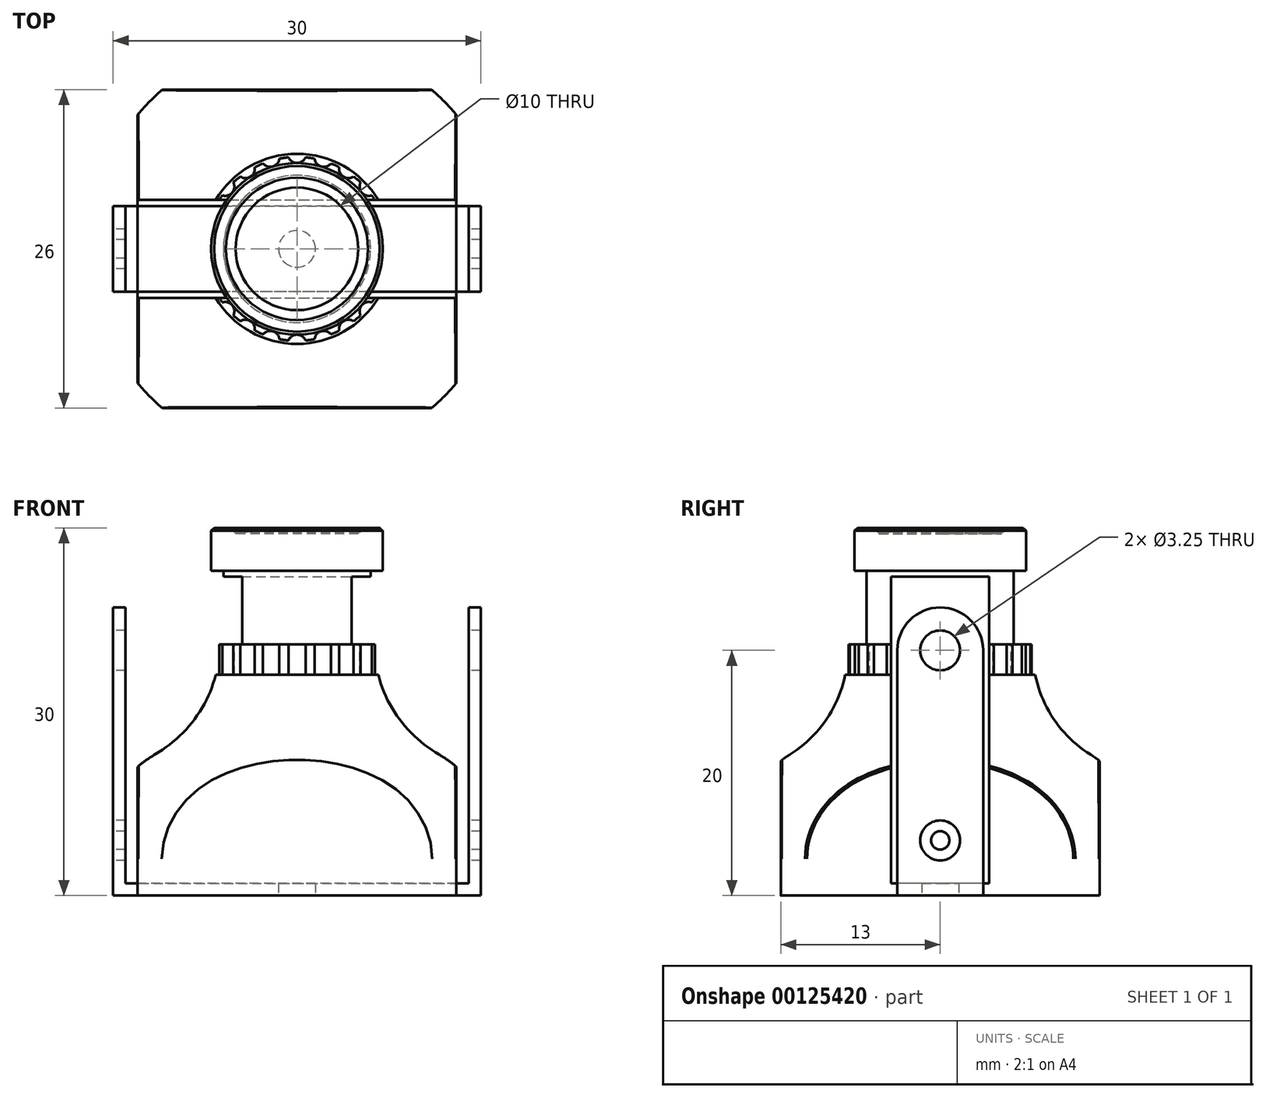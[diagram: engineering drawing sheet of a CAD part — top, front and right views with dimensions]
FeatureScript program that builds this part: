
annotation { "Feature Type Name" : "Feature", "Feature Type Description" : "" }
export const myFeature = defineFeature(function(context is Context, id is Id, definition is map)
    precondition{}
    {
        {
            var Q0;
            Q0=qCreatedBy(makeId("Front.planeOp"),FACE);
            var sketch = newSketch(context, id + "F0", { "sketchPlane" : qUnion([Q0])});
            skLineSegment(sketch, "E0", {"start": v(0, 83.46) * mm, "end": v(0, 0) * mm, "construction": true});
            skLineSegment(sketch, "E1", {"start": v(5, 30) * mm, "end": v(7, 30) * mm});
            skLineSegment(sketch, "E2", {"start": v(7, 30) * mm, "end": v(7, 26.5) * mm});
            skLineSegment(sketch, "E3", {"start": v(7, 26.5) * mm, "end": v(6, 26.5) * mm});
            skLineSegment(sketch, "E4", {"start": v(6, 26.5) * mm, "end": v(6, 20.5) * mm});
            skLineSegment(sketch, "E5", {"start": v(6, 20.5) * mm, "end": v(7.5, 20.5) * mm});
            skLineSegment(sketch, "E6", {"start": v(7.5, 20.5) * mm, "end": v(7.5, 18) * mm});
            skLineSegment(sketch, "E7", {"start": v(7.75, 18) * mm, "end": v(7.5, 18) * mm});
            skLineSegment(sketch, "E8", {"start": v(17, 3) * mm, "end": v(17, 0) * mm});
            skLineSegment(sketch, "E9", {"start": v(17, 0) * mm, "end": v(0, 0) * mm});
            skArc(sketch, "E10", {"start": v(7.75, 18) * mm, "mid": v(9.34, 14.28) * mm, "end": v(12.27, 11.5) * mm});
            skArc(sketch, "E11", {"start": v(17, 3) * mm, "mid": v(15.74, 7.86) * mm, "end": v(12.27, 11.5) * mm});
            skLineSegment(sketch, "E12", {"start": v(5, 30) * mm, "end": v(5, 29.5) * mm});
            skLineSegment(sketch, "E13", {"start": v(0, 29.36) * mm, "end": v(0, 0) * mm});
            skLineSegment(sketch, "E14", {"start": v(0, 29.86) * mm, "end": v(0, 29.36) * mm});
            skArc(sketch, "E15", {"start": v(5, 29.5) * mm, "mid": v(2.5, 29.77) * mm, "end": v(0, 29.86) * mm});
            skSolve(sketch);
        }
        {
            var Q0;
            Q0=makeQuery(id+"F0.imprint","IMPRINT",FACE,{"disambiguationData":[TD([[makeQuery(id+"F0.imprint","IMPRINT",EDGE,{"derivedFrom":sQuery(id+"F0.wireOp",EDGE,"E1")}),-1.0]])]});
            var Q1;
            Q1=sQuery(id+"F0.wireOp",EDGE,"E0");
            revolve(context, id + "F1", {"entities" : qUnion([Q0]), "axis" : qUnion([Q1]), "revolveType" : RevolveType.FULL});
        }
        {
            var Q0;
            Q0=makeQuery(id+"F1.opRevolve","SWEPT_FACE",FACE,{"disambiguationData":[OSD([sQuery(id+"F0.wireOp",EDGE,"E9")])]});
            var sketch = newSketch(context, id + "F2", { "sketchPlane" : qUnion([Q0])});
            skLineSegment(sketch, "E16.bottom", {"start": v(-13, 13) * mm, "end": v(13, 13) * mm});
            skLineSegment(sketch, "E16.top", {"start": v(-13, -13) * mm, "end": v(13, -13) * mm});
            skLineSegment(sketch, "E16.left", {"start": v(-13, 13) * mm, "end": v(-13, -13) * mm});
            skLineSegment(sketch, "E16.right", {"start": v(13, 13) * mm, "end": v(13, -13) * mm});
            skCircle(sketch, "E17", {"center": v(0, 0) * mm, "radius": 20 * mm});
            skSolve(sketch);
        }
        {
            var Q0;
            Q0=qSketchRegion(id+"F2",true);
            extrude(context, id + "F3", {"entities" : qUnion([Q0]), "operationType" : NewBodyOperationType.REMOVE, "oppositeDirection" : true, "depth" : 15 * mm});
        }
        {
            var Q0;
            Q0=makeQuery(id+"F3.boolean.opBoolean","INTERSECT",EDGE,{"disambiguationData":[OD(1.0)],"derivedFrom":[makeQuery(id+"F1.opRevolve","SWEPT_FACE",FACE,{"disambiguationData":[OSD([sQuery(id+"F0.wireOp",EDGE,"E8")])]}),makeQuery(id+"F3.opExtrude","SWEPT_FACE",FACE,{"disambiguationData":[OSD([sQuery(id+"F2.wireOp",EDGE,"E16.left")])]})]});
            var Q1;
            Q1=makeQuery(id+"F3.boolean.opBoolean","INTERSECT",EDGE,{"disambiguationData":[OD(1.0)],"derivedFrom":[makeQuery(id+"F1.opRevolve","SWEPT_FACE",FACE,{"disambiguationData":[OSD([sQuery(id+"F0.wireOp",EDGE,"E11")])]}),makeQuery(id+"F3.opExtrude","SWEPT_FACE",FACE,{"disambiguationData":[OSD([sQuery(id+"F2.wireOp",EDGE,"E16.left")])]})]});
            var Q2;
            Q2=makeQuery(id+"F3.boolean.opBoolean","INTERSECT",EDGE,{"derivedFrom":[makeQuery(id+"F1.opRevolve","SWEPT_FACE",FACE,{"disambiguationData":[OSD([sQuery(id+"F0.wireOp",EDGE,"E10")])]}),makeQuery(id+"F3.opExtrude","SWEPT_FACE",FACE,{"disambiguationData":[OSD([sQuery(id+"F2.wireOp",EDGE,"E16.left")])]})]});
            var Q3;
            Q3=makeQuery(id+"F3.boolean.opBoolean","INTERSECT",EDGE,{"disambiguationData":[OD(0.0)],"derivedFrom":[makeQuery(id+"F1.opRevolve","SWEPT_FACE",FACE,{"disambiguationData":[OSD([sQuery(id+"F0.wireOp",EDGE,"E11")])]}),makeQuery(id+"F3.opExtrude","SWEPT_FACE",FACE,{"disambiguationData":[OSD([sQuery(id+"F2.wireOp",EDGE,"E16.left")])]})]});
            var Q4;
            Q4=makeQuery(id+"F3.boolean.opBoolean","INTERSECT",EDGE,{"disambiguationData":[OD(0.0)],"derivedFrom":[makeQuery(id+"F1.opRevolve","SWEPT_FACE",FACE,{"disambiguationData":[OSD([sQuery(id+"F0.wireOp",EDGE,"E8")])]}),makeQuery(id+"F3.opExtrude","SWEPT_FACE",FACE,{"disambiguationData":[OSD([sQuery(id+"F2.wireOp",EDGE,"E16.left")])]})]});
            var Q5;
            Q5=makeQuery(id+"F3.boolean.opBoolean","INTERSECT",EDGE,{"disambiguationData":[OD(0.0)],"derivedFrom":[makeQuery(id+"F1.opRevolve","SWEPT_FACE",FACE,{"disambiguationData":[OSD([sQuery(id+"F0.wireOp",EDGE,"E8")])]}),makeQuery(id+"F3.opExtrude","SWEPT_FACE",FACE,{"disambiguationData":[OSD([sQuery(id+"F2.wireOp",EDGE,"E16.top")])]})]});
            var Q6;
            Q6=makeQuery(id+"F3.boolean.opBoolean","INTERSECT",EDGE,{"disambiguationData":[OD(1.0)],"derivedFrom":[makeQuery(id+"F1.opRevolve","SWEPT_FACE",FACE,{"disambiguationData":[OSD([sQuery(id+"F0.wireOp",EDGE,"E8")])]}),makeQuery(id+"F3.opExtrude","SWEPT_FACE",FACE,{"disambiguationData":[OSD([sQuery(id+"F2.wireOp",EDGE,"E16.right")])]})]});
            var Q7;
            Q7=makeQuery(id+"F3.boolean.opBoolean","INTERSECT",EDGE,{"disambiguationData":[OD(1.0)],"derivedFrom":[makeQuery(id+"F1.opRevolve","SWEPT_FACE",FACE,{"disambiguationData":[OSD([sQuery(id+"F0.wireOp",EDGE,"E8")])]}),makeQuery(id+"F3.opExtrude","SWEPT_FACE",FACE,{"disambiguationData":[OSD([sQuery(id+"F2.wireOp",EDGE,"E16.bottom")])]})]});
            fillet(context, id + "F4", {"entities" : qUnion([Q0, Q1, Q2, Q3, Q4, Q5, Q6, Q7]), "radius" : 0.25 * mm, "tangentPropagation" : true, "allowEdgeOverflow" : false});
        }
        {
            var Q0;
            Q0=makeQuery(id+"F1.opRevolve","SWEPT_FACE",FACE,{"disambiguationData":[OSD([sQuery(id+"F0.wireOp",EDGE,"E5")])]});
            var sketch = newSketch(context, id + "F5", { "sketchPlane" : qUnion([Q0])});
            skCircle(sketch, "E18", {"center": v(0, 7.75) * mm, "radius": 0.75 * mm});
            skCircle(sketch, "E19.1.0", {"center": v(-2.18, 7.44) * mm, "radius": 0.75 * mm});
            skCircle(sketch, "E19.2.0", {"center": v(-4.19, 6.52) * mm, "radius": 0.75 * mm});
            skCircle(sketch, "E19.3.0", {"center": v(-5.86, 5.08) * mm, "radius": 0.75 * mm});
            skCircle(sketch, "E19.4.0", {"center": v(-7.05, 3.22) * mm, "radius": 0.75 * mm});
            skCircle(sketch, "E19.5.0", {"center": v(-7.67, 1.1) * mm, "radius": 0.75 * mm});
            skCircle(sketch, "E19.6.0", {"center": v(-7.67, -1.1) * mm, "radius": 0.75 * mm});
            skCircle(sketch, "E19.7.0", {"center": v(-7.05, -3.22) * mm, "radius": 0.75 * mm});
            skCircle(sketch, "E19.8.0", {"center": v(-5.86, -5.08) * mm, "radius": 0.75 * mm});
            skCircle(sketch, "E19.9.0", {"center": v(-4.19, -6.52) * mm, "radius": 0.75 * mm});
            skCircle(sketch, "E19.10.0", {"center": v(-2.18, -7.44) * mm, "radius": 0.75 * mm});
            skCircle(sketch, "E19.11.0", {"center": v(0, -7.75) * mm, "radius": 0.75 * mm});
            skCircle(sketch, "E19.12.0", {"center": v(2.18, -7.44) * mm, "radius": 0.75 * mm});
            skCircle(sketch, "E19.13.0", {"center": v(4.19, -6.52) * mm, "radius": 0.75 * mm});
            skCircle(sketch, "E19.14.0", {"center": v(5.86, -5.08) * mm, "radius": 0.75 * mm});
            skCircle(sketch, "E19.15.0", {"center": v(7.05, -3.22) * mm, "radius": 0.75 * mm});
            skCircle(sketch, "E19.16.0", {"center": v(7.67, -1.1) * mm, "radius": 0.75 * mm});
            skCircle(sketch, "E19.17.0", {"center": v(7.67, 1.1) * mm, "radius": 0.75 * mm});
            skCircle(sketch, "E19.18.0", {"center": v(7.05, 3.22) * mm, "radius": 0.75 * mm});
            skCircle(sketch, "E19.19.0", {"center": v(5.86, 5.08) * mm, "radius": 0.75 * mm});
            skCircle(sketch, "E19.20.0", {"center": v(4.19, 6.52) * mm, "radius": 0.75 * mm});
            skCircle(sketch, "E19.21.0", {"center": v(2.18, 7.44) * mm, "radius": 0.75 * mm});
            skPoint(sketch, "E19.center", {"position": v(0, 0) * mm});
            skCircle(sketch, "E20", {"center": v(0, 0) * mm, "radius": 7.75 * mm, "construction": true});
            skLineSegment(sketch, "E21", {"start": v(0, 7.75) * mm, "end": v(0, 0) * mm, "construction": true});
            skLineSegment(sketch, "E22", {"start": v(0, 0) * mm, "end": v(2.18, 7.44) * mm, "construction": true});
            skSolve(sketch);
        }
        {
            var Q0;
            Q0=qSketchRegion(id+"F5",true);
            extrude(context, id + "F6", {"entities" : qUnion([Q0]), "operationType" : NewBodyOperationType.REMOVE, "oppositeDirection" : true, "depth" : 2.5 * mm});
        }
        {
            var Q0;
            Q0=makeQuery(id+"F1.opRevolve","SWEPT_EDGE",EDGE,{"disambiguationData":[OSD([sQuery(id+"F0.wireOp",EDGE,"E1"),sQuery(id+"F0.wireOp",EDGE,"E2")])]});
            chamfer(context, id + "F7", {"entities" : qUnion([Q0]), "width" : 0.25 * mm, "tangentPropagation" : true});
        }
        {
            var Q0;
            Q0=makeQuery(id+"F1.opRevolve","SWEPT_EDGE",EDGE,{"disambiguationData":[OSD([sQuery(id+"F0.wireOp",EDGE,"E1"),sQuery(id+"F0.wireOp",EDGE,"E12")])]});
            chamfer(context, id + "F8", {"entities" : qUnion([Q0]), "chamferType" : ChamferType.TWO_OFFSETS, "width1" : 0.4 * mm, "oppositeDirection" : false, "width2" : 0.8 * mm, "tangentPropagation" : true});
        }
        {
            var Q0;
            Q0=qCreatedBy(makeId("Right.planeOp"),FACE);
            var sketch = newSketch(context, id + "F9", { "sketchPlane" : qUnion([Q0])});
            skCircle(sketch, "E23", {"center": v(0, 4.5) * mm, "radius": 2.25 * mm});
            skSolve(sketch);
        }
        {
            var Q0;
            Q0=qSketchRegion(id+"F9",true);
            extrude(context, id + "F10", {"entities" : qUnion([Q0]), "operationType" : NewBodyOperationType.ADD, "endBound" : BoundingType.SYMMETRIC, "depth" : 28 * mm});
        }
        {
            var Q0;
            Q0=qCreatedBy(makeId("Right.planeOp"),FACE);
            var sketch = newSketch(context, id + "F11", { "sketchPlane" : qUnion([Q0])});
            skCircle(sketch, "E24", {"center": v(0, 4.5) * mm, "radius": 1.63 * mm});
            skCircle(sketch, "E25", {"center": v(0, 4.5) * mm, "radius": 0.75 * mm});
            skSolve(sketch);
        }
        {
            var Q0;
            Q0=qSketchRegion(id+"F11",true);
            extrude(context, id + "F12", {"entities" : qUnion([Q0]), "operationType" : NewBodyOperationType.ADD, "endBound" : BoundingType.SYMMETRIC, "depth" : 30 * mm});
        }
        {
            var Q0;
            Q0=qCreatedBy(makeId("Right.planeOp"),FACE);
            var sketch = newSketch(context, id + "F13", { "sketchPlane" : qUnion([Q0])});
            skArc(sketch, "E26", {"start": v(3.5, 20) * mm, "mid": v(0, 23.5) * mm, "end": v(-3.5, 20) * mm});
            skLineSegment(sketch, "E27", {"start": v(-3.5, 20) * mm, "end": v(-3.5, 0) * mm});
            skLineSegment(sketch, "E28", {"start": v(-3.5, 0) * mm, "end": v(3.5, 0) * mm});
            skLineSegment(sketch, "E29", {"start": v(3.5, 0) * mm, "end": v(3.5, 20) * mm});
            skCircle(sketch, "E30", {"center": v(0, 20) * mm, "radius": 1.63 * mm});
            skSolve(sketch);
        }
        {
            var Q0;
            Q0=qSketchRegion(id+"F13",true);
            extrude(context, id + "F14", {"entities" : qUnion([Q0]), "endBound" : BoundingType.SYMMETRIC, "depth" : 30 * mm});
        }
        {
            var Q0;
            Q0=qCreatedBy(makeId("Front.planeOp"),FACE);
            var sketch = newSketch(context, id + "F15", { "sketchPlane" : qUnion([Q0])});
            skLineSegment(sketch, "E31.bottom", {"start": v(-14, 26) * mm, "end": v(14, 26) * mm});
            skLineSegment(sketch, "E31.top", {"start": v(-14, 1) * mm, "end": v(14, 1) * mm});
            skLineSegment(sketch, "E31.left", {"start": v(-14, 26) * mm, "end": v(-14, 1) * mm});
            skLineSegment(sketch, "E31.right", {"start": v(14, 26) * mm, "end": v(14, 1) * mm});
            skSolve(sketch);
        }
        {
            var Q0;
            Q0=qSketchRegion(id+"F15",true);
            extrude(context, id + "F16", {"entities" : qUnion([Q0]), "operationType" : NewBodyOperationType.REMOVE, "endBound" : BoundingType.SYMMETRIC, "oppositeDirection" : true, "depth" : 8 * mm});
        }
        {
            var Q0;
            Q0=qCreatedBy(makeId("Top.planeOp"),FACE);
            var sketch = newSketch(context, id + "F17", { "sketchPlane" : qUnion([Q0])});
            skCircle(sketch, "E32", {"center": v(0, 0) * mm, "radius": 1.5 * mm});
            skSolve(sketch);
        }
        {
            var Q0;
            Q0=qSketchRegion(id+"F17",true);
            extrude(context, id + "F18", {"entities" : qUnion([Q0]), "operationType" : NewBodyOperationType.REMOVE, "depth" : 2 * mm});
        }
    });
